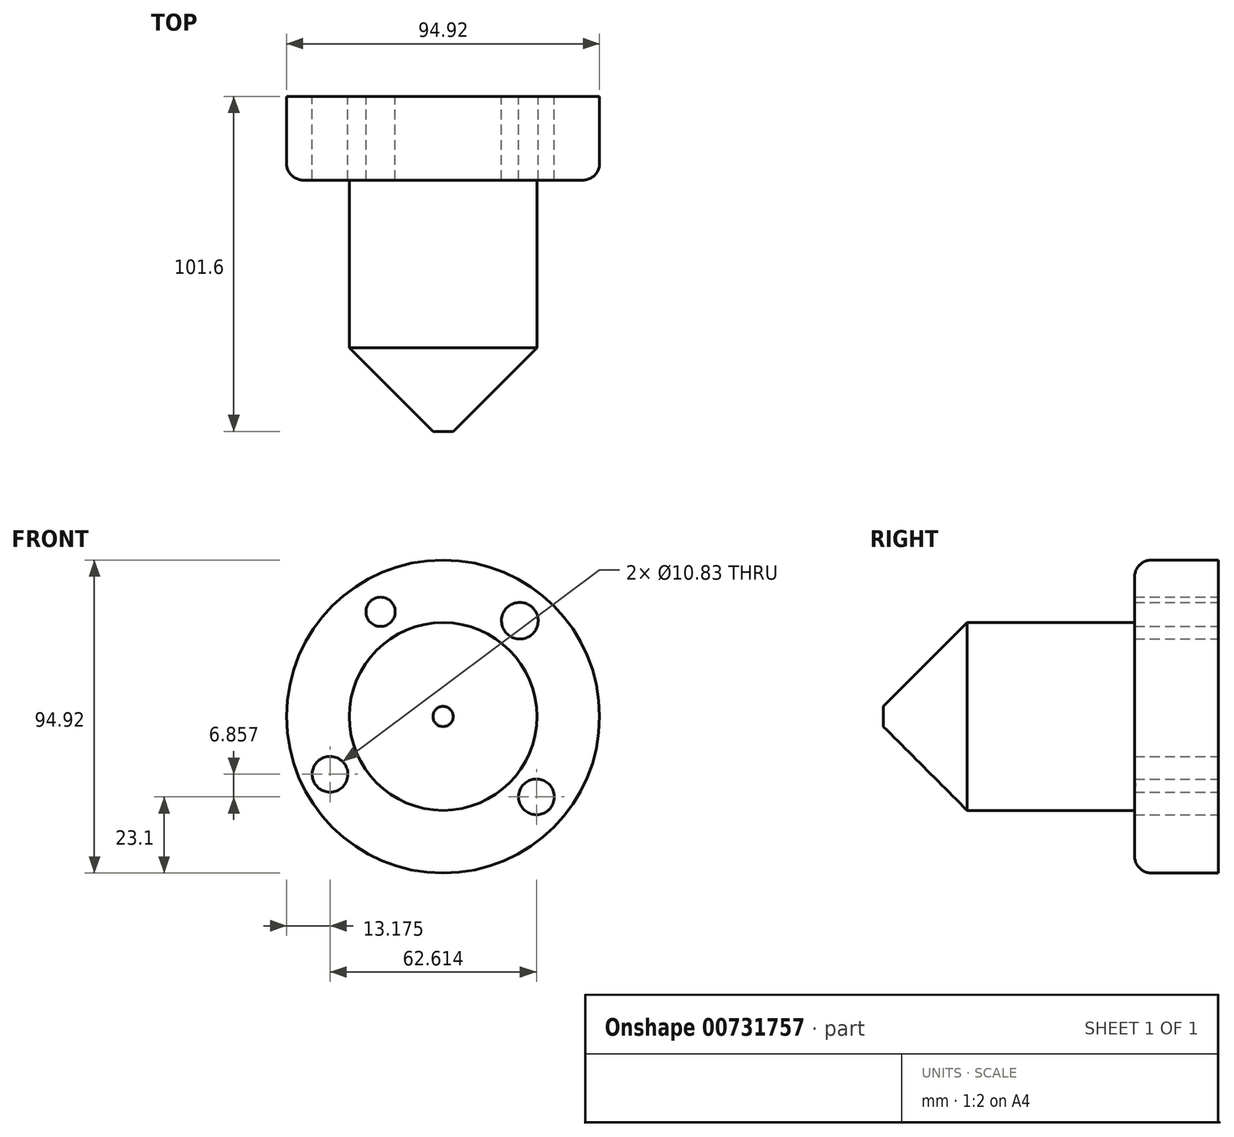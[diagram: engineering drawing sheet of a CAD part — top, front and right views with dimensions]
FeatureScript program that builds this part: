
annotation { "Feature Type Name" : "Feature", "Feature Type Description" : "" }
export const myFeature = defineFeature(function(context is Context, id is Id, definition is map)
    precondition{}
    {
        {
            var Q0;
            Q0=qCreatedBy(makeId("Front.planeOp"),FACE);
            var sketch = newSketch(context, id + "F0", { "sketchPlane" : qUnion([Q0])});
            skCircle(sketch, "E0", {"center": v(0, 0) * mm, "radius": 47.46 * mm});
            skCircle(sketch, "E1", {"center": v(0, 0) * mm, "radius": 28.34 * mm});
            skCircle(sketch, "E2", {"center": v(-18.95, 31.76) * mm, "radius": 4.44 * mm});
            skCircle(sketch, "E3", {"center": v(28.33, -24.36) * mm, "radius": 5.42 * mm});
            skCircle(sketch, "E4", {"center": v(23.28, 29.05) * mm, "radius": 5.56 * mm});
            skCircle(sketch, "E5", {"center": v(-34.28, -17.5) * mm, "radius": 5.41 * mm});
            skSolve(sketch);
        }
        {
            var Q0;
            Q0=makeQuery(id+"F0.imprint","IMPRINT",FACE,{"disambiguationData":[TD([[makeQuery(id+"F0.imprint","IMPRINT",EDGE,{"derivedFrom":sQuery(id+"F0.wireOp",EDGE,"E0")}),1.0]])]});
            var Q1;
            Q1 = qSketchRegion(id + "F0", true);
            extrude(context, id + "F1", {"entities" : qUnion([Q0, Q1]), "depth" : 25.4 * mm, "offsetDistance" : 25.4 * mm});
        }
        {
            var Q0;
            Q0=qCreatedBy(makeId("Front.planeOp"),FACE);
            var sketch = newSketch(context, id + "F2", { "sketchPlane" : qUnion([Q0])});
            skCircle(sketch, "E6", {"center": v(0, 0) * mm, "radius": 28.46 * mm});
            skSolve(sketch);
        }
        {
            var Q0;
            Q0=makeQuery(id+"F2.imprint","IMPRINT",FACE,{"disambiguationData":[TD([[makeQuery(id+"F2.imprint","IMPRINT",EDGE,{"derivedFrom":sQuery(id+"F2.wireOp",EDGE,"E6")}),1.0]])]});
            var Q1;
            Q1 = qSketchRegion(id + "F2", true);
            extrude(context, id + "F3", {"entities" : qUnion([Q0, Q1]), "operationType" : NewBodyOperationType.ADD, "depth" : 101.6 * mm, "offsetDistance" : 25.4 * mm});
        }
        {
            var Q0;
            Q0=makeQuery(id+"F3.opExtrude","CAP_FACE",FACE,{"disambiguationData":[OSD([sQuery(id+"F2.wireOp",EDGE,"E6")])],"isStart":false});
            chamfer(context, id + "F4", {"entities" : qUnion([Q0]), "width" : 25.4 * mm, "tangentPropagation" : true});
        }
        {
            var Q0;
            Q0=makeQuery(id+"F1.opExtrude","CAP_EDGE",EDGE,{"disambiguationData":[OSD([sQuery(id+"F0.wireOp",EDGE,"E0")])],"isStart":false});
            fillet(context, id + "F5", {"entities" : qUnion([Q0]), "radius" : 5.08 * mm, "tangentPropagation" : true, "allowEdgeOverflow" : false});
        }
    });
